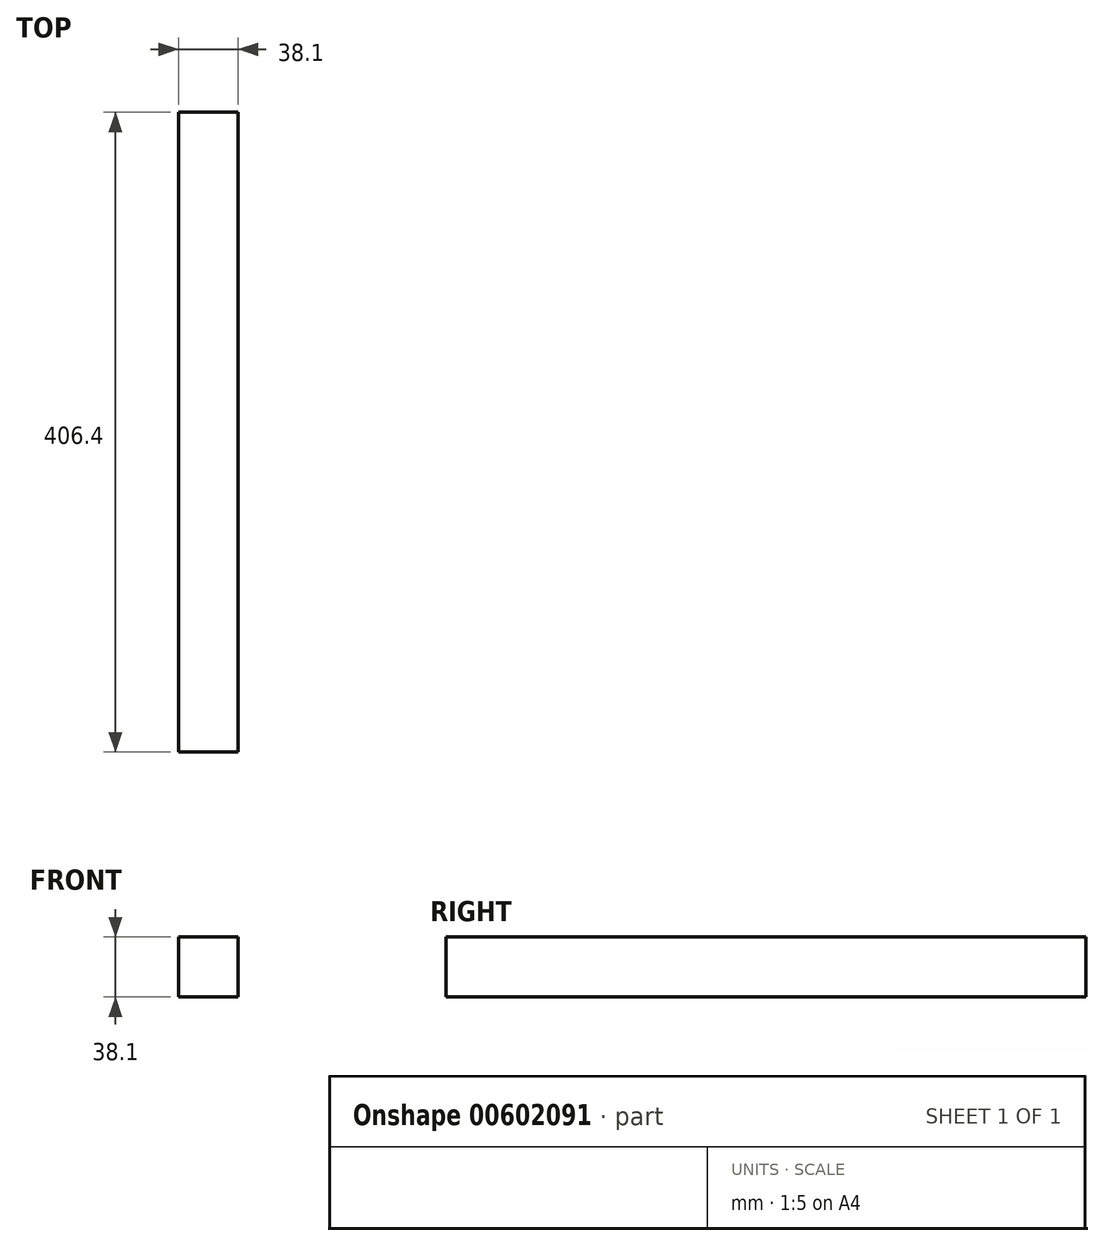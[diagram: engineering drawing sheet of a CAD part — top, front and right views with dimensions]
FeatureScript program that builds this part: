
annotation { "Feature Type Name" : "Feature", "Feature Type Description" : "" }
export const myFeature = defineFeature(function(context is Context, id is Id, definition is map)
    precondition{}
    {
        {
            var Q0;
            Q0=qCreatedBy(makeId("Front.planeOp"),FACE);
            var sketch = newSketch(context, id + "F0", { "sketchPlane" : qUnion([Q0])});
            skLineSegment(sketch, "E0.bottom", {"start": v(19.05, 19.05) * mm, "end": v(-19.05, 19.05) * mm});
            skLineSegment(sketch, "E0.top", {"start": v(19.05, -19.05) * mm, "end": v(-19.05, -19.05) * mm});
            skLineSegment(sketch, "E0.left", {"start": v(19.05, 19.05) * mm, "end": v(19.05, -19.05) * mm});
            skLineSegment(sketch, "E0.right", {"start": v(-19.05, 19.05) * mm, "end": v(-19.05, -19.05) * mm});
            skPoint(sketch, "E0.middle", {"position": v(0, 0) * mm});
            skSolve(sketch);
        }
        {
            var Q0;
            Q0=makeQuery(id+"F0.imprint","IMPRINT",FACE,{"disambiguationData":[TD([[makeQuery(id+"F0.imprint","IMPRINT",EDGE,{"derivedFrom":sQuery(id+"F0.wireOp",EDGE,"E0.bottom")}),1.0]])]});
            extrude(context, id + "F1", {"entities" : qUnion([Q0]), "depth" : 406.4 * mm, "offsetDistance" : 25.4 * mm});
        }
    });
